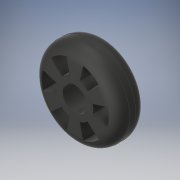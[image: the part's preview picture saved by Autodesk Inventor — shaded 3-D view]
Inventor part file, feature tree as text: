
AUTODESK INVENTOR PART (.ipt)
format: ipt  version: 2017 SP1 (Build 210196100, 196)  size: 229,376 bytes
history: native  units: in
note: dims shown in document units (in); Inventor stores cm internally (conversion verified against a paired STEP export)
features: extrude x1, fillet x1, sketch x1
ambient origin geometry x8: Origin, YZ Plane, XZ Plane, XY Plane, X Axis, Y Axis, Z Axis, Center Point
bodies: Solid1 (feature_tree)
feature tree (3):
  extrude  "Extrusion1"  Depth=0.0787in
  fillet  "Fillet1"  Radius=0.2362in
  sketch  "Sketch1"  dims[d0=0.1575in d1=0.5512in d2=0.2362in d3=0.4331in d4=0.0295in d5=0.0295in d6=2.3622in d8=360.0deg d10=0.1969in d11=0.0in d12=0.0787in]
